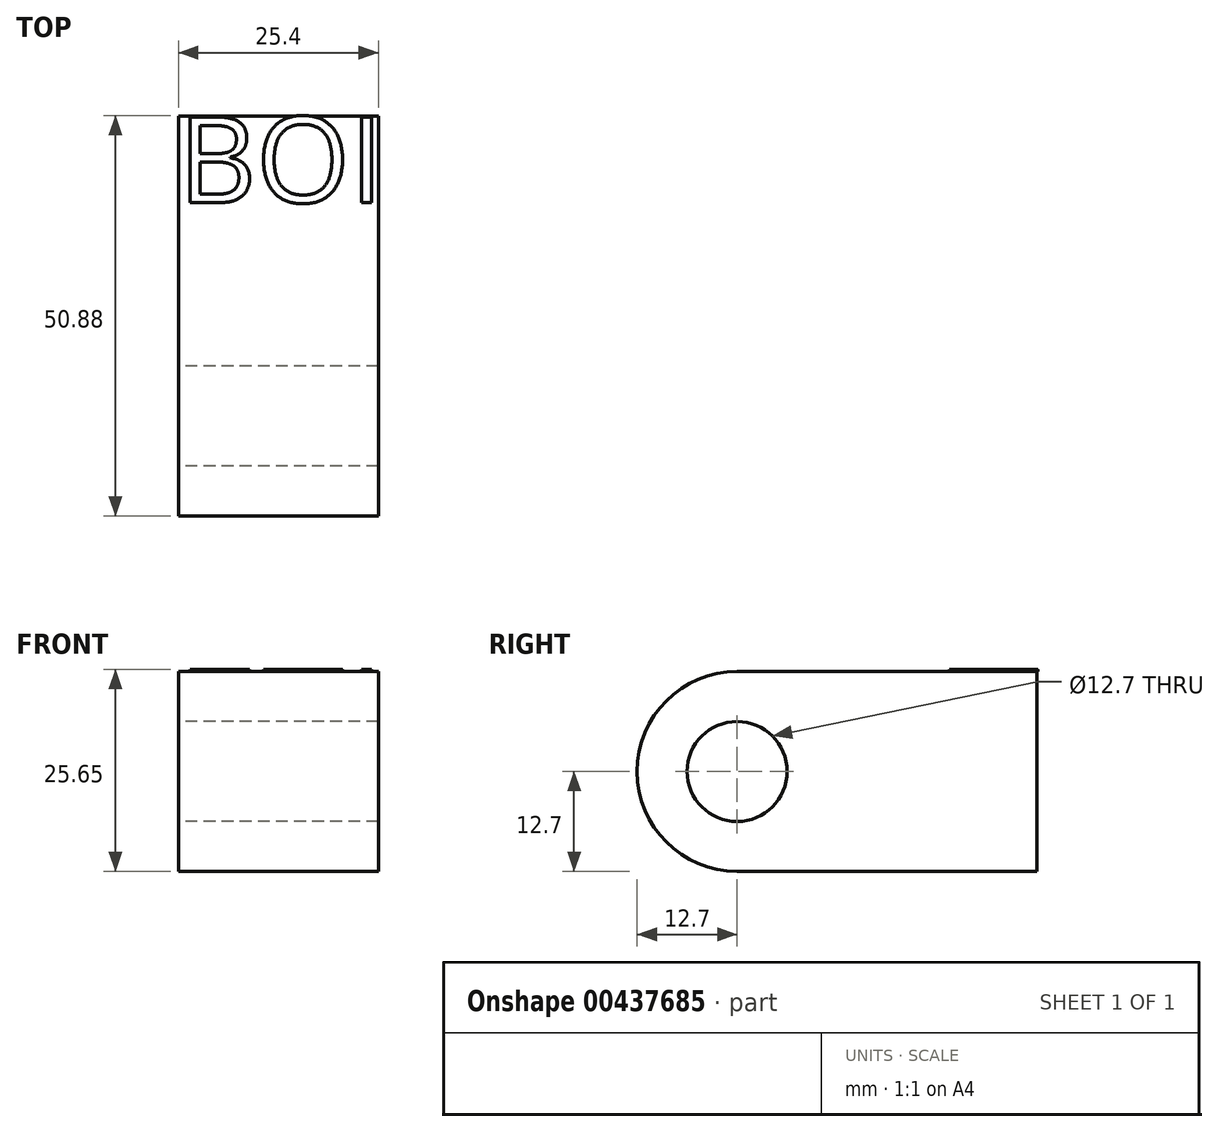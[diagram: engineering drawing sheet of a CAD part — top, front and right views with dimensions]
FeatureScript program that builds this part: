
annotation { "Feature Type Name" : "Feature", "Feature Type Description" : "" }
export const myFeature = defineFeature(function(context is Context, id is Id, definition is map)
    precondition{}
    {
        {
            var Q0;
            Q0=qCreatedBy(makeId("Front.planeOp"),FACE);
            var sketch = newSketch(context, id + "F0", { "sketchPlane" : qUnion([Q0])});
            skLineSegment(sketch, "E0.bottom", {"start": v(-12.7, 12.7) * mm, "end": v(12.7, 12.7) * mm});
            skLineSegment(sketch, "E0.top", {"start": v(-12.7, -12.7) * mm, "end": v(12.7, -12.7) * mm});
            skLineSegment(sketch, "E0.left", {"start": v(-12.7, 12.7) * mm, "end": v(-12.7, -12.7) * mm});
            skLineSegment(sketch, "E0.right", {"start": v(12.7, 12.7) * mm, "end": v(12.7, -12.7) * mm});
            skPoint(sketch, "E0.middle", {"position": v(0, 0) * mm});
            skSolve(sketch);
        }
        {
            var Q0;
            Q0=makeQuery(id+"F0.imprint","IMPRINT",FACE,{"disambiguationData":[TD([[makeQuery(id+"F0.imprint","IMPRINT",EDGE,{"derivedFrom":sQuery(id+"F0.wireOp",EDGE,"E0.bottom")}),-1.0]])]});
            extrude(context, id + "F1", {"entities" : qUnion([Q0]), "depth" : 50.8 * mm});
        }
        {
            var Q0;
            Q0=makeQuery(id+"F1.opExtrude","SWEPT_FACE",FACE,{"disambiguationData":[OSD([sQuery(id+"F0.wireOp",EDGE,"E0.left")])]});
            var sketch = newSketch(context, id + "F2", { "sketchPlane" : qUnion([Q0])});
            skCircle(sketch, "E1", {"center": v(38.1, 0) * mm, "radius": 6.35 * mm});
            skSolve(sketch);
        }
        {
            var Q0;
            Q0=makeQuery(id+"F1.opExtrude","CAP_EDGE",EDGE,{"disambiguationData":[OSD([sQuery(id+"F0.wireOp",EDGE,"E0.bottom")])],"isStart":false});
            var Q1;
            Q1=makeQuery(id+"F1.opExtrude","CAP_EDGE",EDGE,{"disambiguationData":[OSD([sQuery(id+"F0.wireOp",EDGE,"E0.top")])],"isStart":false});
            fillet(context, id + "F3", {"entities" : qUnion([Q0, Q1]), "radius" : 12.7 * mm, "tangentPropagation" : true, "allowEdgeOverflow" : false});
        }
        {
            var Q0;
            Q0=makeQuery(id+"F2.imprint","IMPRINT",FACE,{"disambiguationData":[TD([[makeQuery(id+"F2.imprint","IMPRINT",EDGE,{"derivedFrom":sQuery(id+"F2.wireOp",EDGE,"E1")}),1.0]])]});
            extrude(context, id + "F4", {"entities" : qUnion([Q0]), "operationType" : NewBodyOperationType.REMOVE, "oppositeDirection" : true, "depth" : 25.4 * mm});
        }
        {
            var Q0;
            Q0=makeQuery(id+"F1.opExtrude","SWEPT_FACE",FACE,{"disambiguationData":[OSD([sQuery(id+"F0.wireOp",EDGE,"E0.bottom")])]});
            var sketch = newSketch(context, id + "F5", { "sketchPlane" : qUnion([Q0])});
            skText(sketch, "E2", { "text": "BOI\n", "fontName": "OpenSans-Regular.ttf"});
            const initialGuessF5  = {"E2": [-0.0127, -0.01099, 1, 0, 0.01099]};
            skSetInitialGuess(sketch, initialGuessF5);
            skSolve(sketch);
        }
        {
            var Q0;
            Q0 = qSketchRegion(id + "F5", true);
            extrude(context, id + "F6", {"entities" : qUnion([Q0]), "operationType" : NewBodyOperationType.ADD, "depth" : 0.25 * mm});
        }
    });
